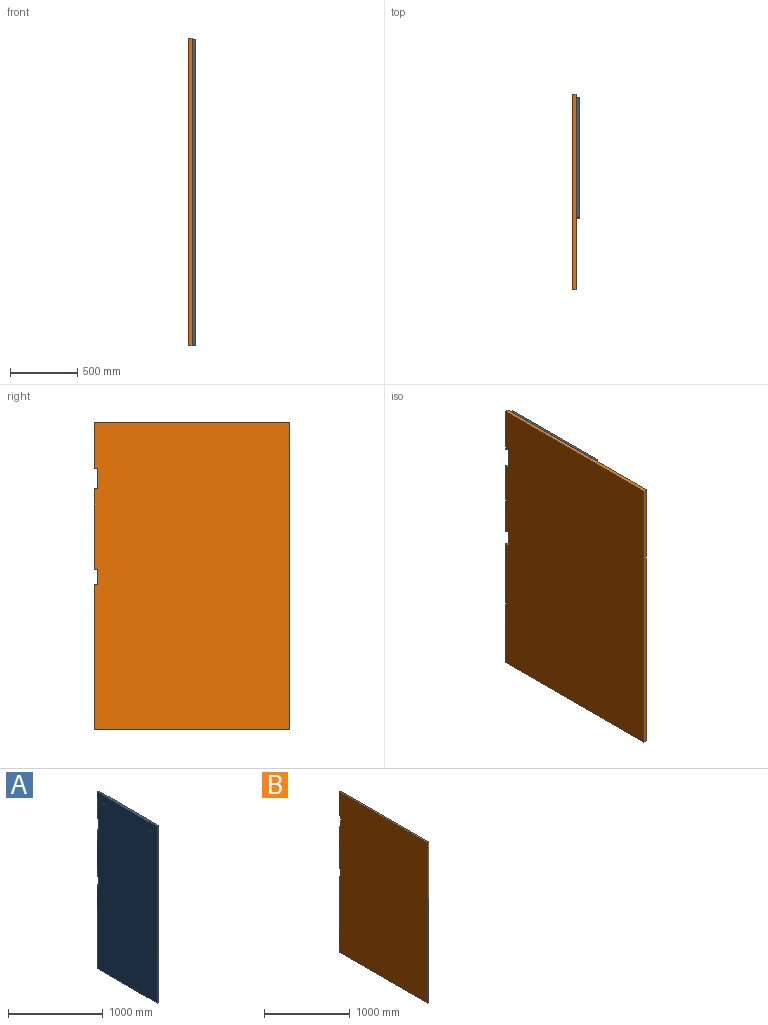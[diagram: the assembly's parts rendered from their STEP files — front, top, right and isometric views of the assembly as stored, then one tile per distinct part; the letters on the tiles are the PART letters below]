
ASSEMBLY  parts=2 mates=1
PART A: 16 faces, bbox 25.4x895.4x2280.4 mm
  f0: plane 895.35x25.4mm, normal (0,0,-1), area 22741.9mm2, adj f1,f13,f14,f15
  f1: plane 1079.5x25.4mm, normal (0,1,0), area 27419.3mm2, adj f0,f2,f14,f15
  f2: plane 25.4x25.4mm, normal (0,0,1), area 645.2mm2, adj f1,f3,f14,f15
  f3: plane 114.3x25.4mm, normal (0,1,0), area 2903.2mm2, adj f2,f4,f14,f15
  f4: plane 25.4x25.4mm, normal (0,0,-1), area 645.2mm2, adj f3,f5,f14,f15
  f5: plane 596.9x25.4mm, normal (0,1,0), area 15161.3mm2, adj f4,f6,f14,f15
  f6: plane 25.4x25.4mm, normal (0,0,1), area 645.2mm2, adj f5,f7,f14,f15
  f7: plane 152.4x25.4mm, normal (0,1,0), area 3871mm2, adj f6,f8,f14,f15
  f8: plane 25.4x25.4mm, normal (0,0,-1), area 645.2mm2, adj f7,f9,f14,f15
  f9: plane 337.31x25.4mm, normal (0,1,0), area 8567.7mm2, adj f8,f10,f14,f15
  f10: plane 895.35x25.4mm, normal (0,0,1), area 22741.9mm2, adj f9,f13,f14,f15
  f11: cylinder r=6.35mm len=25.4mm, axis (-1,0,0), area 1013.4mm2, adj f14,f15
  f12: cylinder r=6.35mm len=25.4mm, axis (-1,0,0), area 1013.4mm2, adj f14,f15
  f13: plane 2280.41x25.4mm, normal (0,-1,0), area 57922.5mm2, adj f0,f10,f14,f15
  f14: plane 2280.41x895.35mm, normal (1,0,0), area 2034739.3mm2, adj f0,f1,f2,f3,f4,f5,f6,f7
  f15: plane 2280.41x895.35mm, normal (-1,0,0), area 2034739.3mm2, adj f0,f1,f2,f3,f4,f5,f6,f7
PART B: 14 faces, bbox 25.4x1454.2x2286 mm
  f0: plane 25.4x25.4mm, normal (0,0,-1), area 645.2mm2, adj f1,f11,f12,f13
  f1: plane 342.9x25.4mm, normal (0,1,0), area 8709.7mm2, adj f0,f2,f12,f13
  f2: plane 1454.15x25.4mm, normal (0,0,1), area 36935.4mm2, adj f1,f3,f12,f13
  f3: plane 2286x25.4mm, normal (0,-1,0), area 58064.4mm2, adj f2,f4,f12,f13
  f4: plane 1454.15x25.4mm, normal (0,0,-1), area 36935.4mm2, adj f3,f5,f12,f13
  f5: plane 1079.5x25.4mm, normal (0,1,0), area 27419.3mm2, adj f4,f6,f12,f13
  f6: plane 25.4x25.4mm, normal (0,0,1), area 645.2mm2, adj f5,f7,f12,f13
  f7: plane 114.3x25.4mm, normal (0,1,0), area 2903.2mm2, adj f6,f8,f12,f13
  f8: plane 25.4x25.4mm, normal (0,0,-1), area 645.2mm2, adj f7,f9,f12,f13
  f9: plane 596.9x25.4mm, normal (0,1,0), area 15161.3mm2, adj f8,f10,f12,f13
  f10: plane 25.4x25.4mm, normal (0,0,1), area 645.2mm2, adj f9,f11,f12,f13
  f11: plane 152.4x25.4mm, normal (0,1,0), area 3871mm2, adj f0,f10,f12,f13
  f12: plane 2286x1454.15mm, normal (-1,0,0), area 3317412.7mm2, adj f0,f1,f2,f3,f4,f5,f6,f7
  f13: plane 2286x1454.15mm, normal (1,0,0), area 3317412.7mm2, adj f0,f1,f2,f3,f4,f5,f6,f7
PLACE A t=(0,-919.65,0)mm
PLACE B at identity fixed
MATE slider A.f1 <-> B.f5  axis (0,1,0) through (0,-24.3,0)mm
